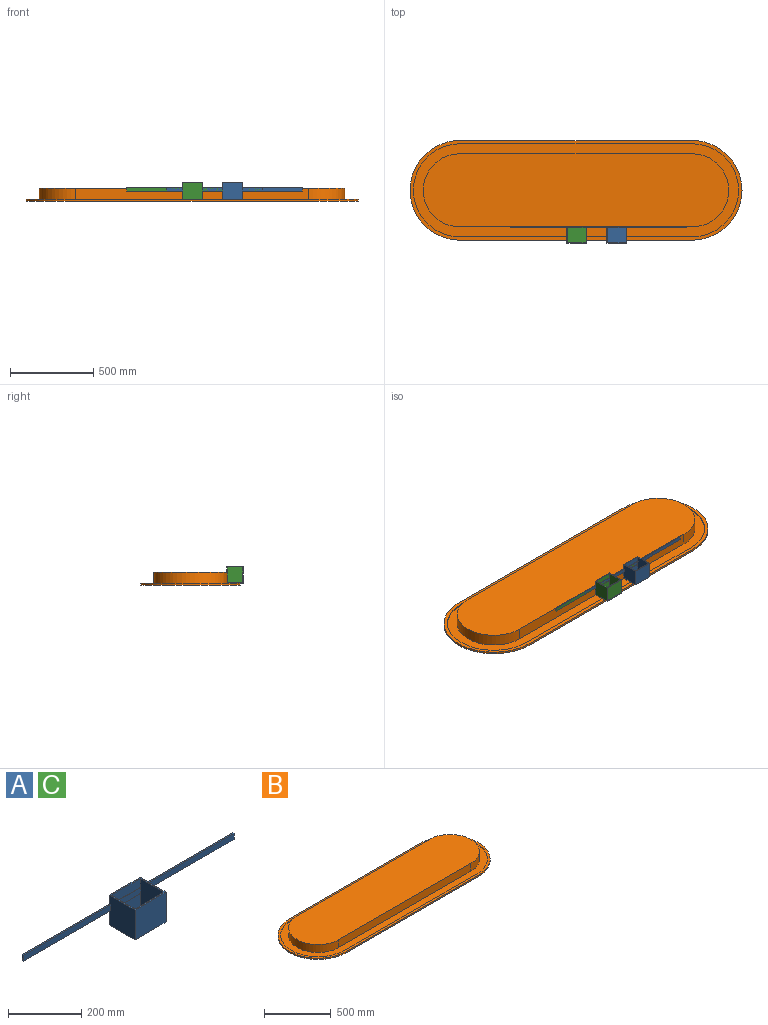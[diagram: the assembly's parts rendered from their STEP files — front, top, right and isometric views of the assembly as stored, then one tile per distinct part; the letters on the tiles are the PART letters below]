
ASSEMBLY  parts=3 mates=4
PART A: 23 faces, bbox 816.3x100x100 mm
  f0: plane 100x100mm, normal (-1,0,0), area 9900mm2, adj f5,f6,f7,f8,f19,f20,f22
  f1: plane 100x100mm, normal (1,0,0), area 9900mm2, adj f5,f6,f7,f8,f16,f17,f18
  f2: plane 112x30mm, normal (0,-1,0), area 3360mm2, adj f3,f4,f5,f14
  f3: plane 96x92mm, normal (1,0,0), area 8812mm2, adj f2,f5,f9,f10,f11,f12,f13,f14
  f4: plane 96x92mm, normal (-1,0,0), area 8812mm2, adj f2,f5,f9,f10,f11,f12,f13,f14
  f5: plane 120x100mm, normal (0,0,1), area 1696mm2, adj f0,f1,f2,f3,f4,f6,f7,f10
  f6: plane 816.27x100mm, normal (0,1,0), area 25925.3mm2, adj f0,f1,f5,f8,f15,f17,f18,f19
  f7: plane 120x100mm, normal (0,-1,0), area 12000mm2, adj f0,f1,f5,f8
  f8: plane 120x100mm, normal (0,0,-1), area 12000mm2, adj f0,f1,f6,f7
  f9: plane 112x46mm, normal (0,-1,0), area 5152mm2, adj f3,f4,f11,f13
  f10: plane 112x96mm, normal (0,1,0), area 10752mm2, adj f3,f4,f5,f11
  f11: plane 112x92mm, normal (0,0,1), area 10304mm2, adj f3,f4,f9,f10
  f12: plane 112x20mm, normal (0,-1,0), area 2240mm2, adj f3,f4,f13,f14
  f13: plane 112x1mm, normal (0,0,-1), area 112mm2, adj f3,f4,f9,f12
  f14: plane 112x1mm, normal (0,0,1), area 112mm2, adj f2,f3,f4,f12
  f15: plane 20x5mm, normal (1,0,0), area 100mm2, adj f6,f16,f17,f18
  f16: plane 358.13x20mm, normal (0,-1,0), area 7162.6mm2, adj f1,f15,f17,f18
  f17: plane 358.13x5mm, normal (0,0,-1), area 1790.6mm2, adj f1,f6,f15,f16
  f18: plane 358.13x5mm, normal (0,0,1), area 1790.6mm2, adj f1,f6,f15,f16
  f19: plane 338.14x5mm, normal (0,0,1), area 1690.7mm2, adj f0,f6,f21,f22
  f20: plane 338.14x5mm, normal (0,0,-1), area 1690.7mm2, adj f0,f6,f21,f22
  f21: plane 20x5mm, normal (-1,0,0), area 100mm2, adj f6,f19,f20,f22
  f22: plane 338.14x20mm, normal (0,-1,0), area 6762.7mm2, adj f0,f19,f20,f21
PART B: 16 faces, bbox 2000x600x80 mm
  f0: plane 1400x72mm, normal (0,-1,0), area 100800mm2, adj f1,f3,f4,f5
  f1: cylinder r=220mm len=440mm, axis (0,0,-1), area 49762.8mm2, adj f0,f2,f4,f5
  f2: plane 1400x72mm, normal (0,1,0), area 100800mm2, adj f1,f3,f4,f5
  f3: cylinder r=220mm len=440mm, axis (0,0,-1), area 49762.8mm2, adj f0,f2,f4,f5
  f4: plane 1840x440mm, normal (0,0,1), area 768053.1mm2, adj f0,f1,f2,f3
  f5: plane 1960x560mm, normal (0,0,1), area 262247.8mm2, adj f0,f1,f2,f3,f6,f7,f8,f9
  f6: plane 1400x4mm, normal (0,1,0), area 5600mm2, adj f5,f8,f9,f14
  f7: plane 1400x4mm, normal (0,-1,0), area 5600mm2, adj f5,f8,f9,f14
  f8: cylinder r=280mm len=560mm, axis (0,0,-1), area 3518.6mm2, adj f5,f6,f7,f14
  f9: cylinder r=280mm len=560mm, axis (0,0,-1), area 3518.6mm2, adj f5,f6,f7,f14
  f10: plane 1400x12mm, normal (0,1,0), area 16800mm2, adj f11,f13,f14,f15
  f11: cylinder r=300mm len=600mm, axis (0,0,-1), area 11309.7mm2, adj f10,f12,f14,f15
  f12: plane 1400x12mm, normal (0,-1,0), area 16800mm2, adj f11,f13,f14,f15
  f13: cylinder r=300mm len=600mm, axis (0,0,-1), area 11309.7mm2, adj f10,f12,f14,f15
  f14: plane 2000x600mm, normal (0,0,1), area 92442.4mm2, adj f6,f7,f8,f9,f10,f11,f12,f13
  f15: plane 2000x600mm, normal (0,0,-1), area 1122743.3mm2, adj f10,f11,f12,f13
PART C: same geometry as A
PLACE A t=(483.21,448.08,0.04)mm
PLACE B t=(200.65,405.97,-11.96)mm fixed
PLACE C t=(241.39,448.08,0.04)mm
MATE planar B.f0 <-> C.f6  axis (0,-1,0) through (202.41,529.52,32.04)mm
MATE planar A.f6 <-> B.f0  axis (0,1,0) through (455.44,529.52,55.42)mm
MATE planar C.f8 <-> B.f14  axis (0,0,-1) through (207.32,479.52,0.04)mm
MATE planar A.f8 <-> B.f14  axis (0,0,-1) through (449.14,479.52,0.04)mm
